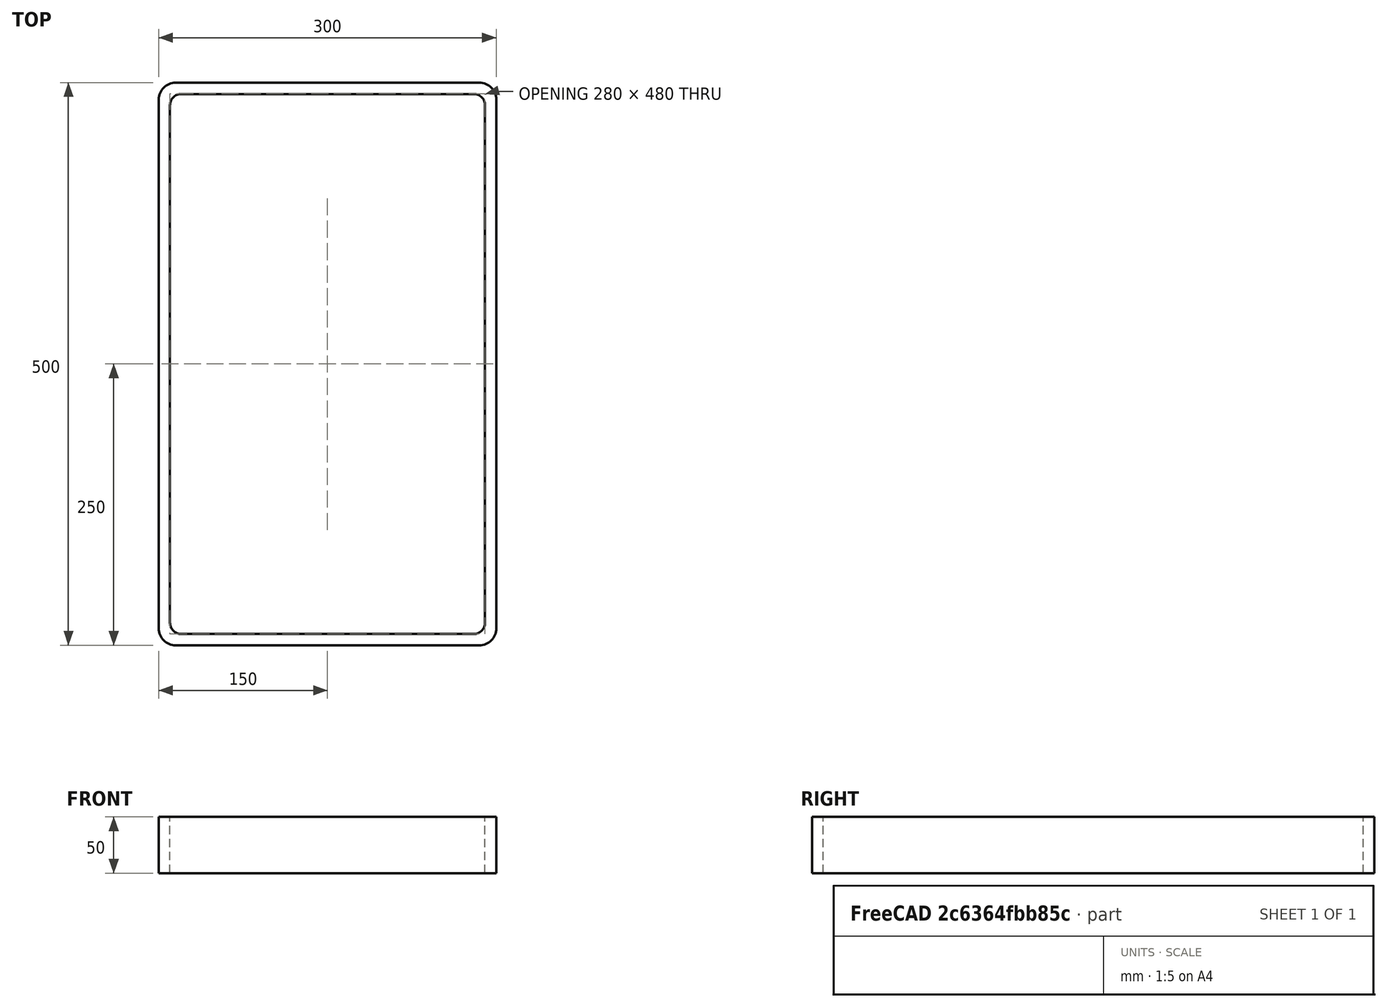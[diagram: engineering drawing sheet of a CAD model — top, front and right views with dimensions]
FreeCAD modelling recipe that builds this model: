
FCSTD DOCUMENT  (FreeCAD 0.15R4671 (Git))
Label: Rectangular hollow section 500x300x10 EN10219 S235JRH
License: All rights reserved
LicenseURL: http://en.wikipedia.org/wiki/All_rights_reserved
objects: Sketcher::SketchObject×1, Part::Extrusion×1
note: 2 computed .brp shape members not serialized (recipe doc carries the construction recipe); baked Part::Feature solids carry a one-line shape summary decoded from their .brp

FEATURE [Sketcher::SketchObject] Sketch
  sketch-geometry (16):
    g0: LineSegment StartX=-130 StartY=240 StartZ=0 EndX=130 EndY=240 EndZ=0
    g1: LineSegment StartX=140 StartY=230 StartZ=0 EndX=140 EndY=-230 EndZ=0
    g2: LineSegment StartX=130 StartY=-240 StartZ=0 EndX=-130 EndY=-240 EndZ=0
    g3: LineSegment StartX=-140 StartY=-230 StartZ=0 EndX=-140 EndY=230 EndZ=0
    g4: LineSegment StartX=-135 StartY=250 StartZ=0 EndX=135 EndY=250 EndZ=0
    g5: LineSegment StartX=150 StartY=235 StartZ=0 EndX=150 EndY=-235 EndZ=0
    g6: LineSegment StartX=135 StartY=-250 StartZ=0 EndX=-135 EndY=-250 EndZ=0
    g7: LineSegment StartX=-150 StartY=-235 StartZ=0 EndX=-150 EndY=235 EndZ=0
    g8: ArcOfCircle CenterX=-130 CenterY=230 CenterZ=0 NormalX=0 NormalY=0 NormalZ=1 Radius=10 StartAngle=1.5708 EndAngle=3.14159
    g9: ArcOfCircle CenterX=130 CenterY=230 CenterZ=0 NormalX=0 NormalY=0 NormalZ=1 Radius=10 StartAngle=0 EndAngle=1.5708
    g10: ArcOfCircle CenterX=130 CenterY=-230 CenterZ=0 NormalX=0 NormalY=0 NormalZ=1 Radius=10 StartAngle=4.71239 EndAngle=6.28319
    g11: ArcOfCircle CenterX=-130 CenterY=-230 CenterZ=0 NormalX=0 NormalY=0 NormalZ=1 Radius=10 StartAngle=3.14159 EndAngle=4.71239
    g12: ArcOfCircle CenterX=135 CenterY=235 CenterZ=0 NormalX=0 NormalY=0 NormalZ=1 Radius=15 StartAngle=0 EndAngle=1.5708
    g13: ArcOfCircle CenterX=135 CenterY=-235 CenterZ=0 NormalX=0 NormalY=0 NormalZ=1 Radius=15 StartAngle=4.71239 EndAngle=6.28319
    g14: ArcOfCircle CenterX=-135 CenterY=-235 CenterZ=0 NormalX=0 NormalY=0 NormalZ=1 Radius=15 StartAngle=3.14159 EndAngle=4.71239
    g15: ArcOfCircle CenterX=-135 CenterY=235 CenterZ=0 NormalX=0 NormalY=0 NormalZ=1 Radius=15 StartAngle=1.5708 EndAngle=3.14159
  constraints (36):
    c: Horizontal(g2)
    c: Vertical(g3)
    c: Horizontal(g6)
    c: Vertical(g7)
    c: Tangent(g3,g8) = 1.5708
    c: Tangent(g0,g8) = 1.5708
    c: Tangent(g0,g9) = 1.5708
    c: Tangent(g1,g9) = 1.5708
    c: Tangent(g1,g10) = 1.5708
    c: Tangent(g2,g10) = 1.5708
    c: Tangent(g2,g11) = 1.5708
    c: Tangent(g3,g11) = 1.5708
    c: Tangent(g4,g12) = 1.5708
    c: Tangent(g5,g12) = 1.5708
    c: Tangent(g5,g13) = 1.5708
    c: Tangent(g6,g13) = 1.5708
    c: Tangent(g6,g14) = 1.5708
    c: Tangent(g7,g14) = 1.5708
    c: Tangent(g7,g15) = 1.5708
    c: Tangent(g4,g15) = 1.5708
    c: Equal(g9,g8)
    c: Equal(g9,g11)
    c: Equal(g9,g10)
    c: Equal(g12,g15)
    c: Equal(g12,g14)
    c: Equal(g12,g13)
    c: Symmetric(g4,g6,g-1)
    c: Symmetric(g7,g5,g-2)
    c: DistanceY(g4,g6) = -500
    c: DistanceX(g7,g5) = 300
    c: Symmetric(g3,g1,g-2)
    c: Symmetric(g0,g2,g-1)
    c: DistanceY(g0,g4) = 10
    c: DistanceX(g5,g1) = -10
    c: Radius(g9) = 10
    c: Radius(g12) = 15
FEATURE [Part::Extrusion] Extrude  label="Rectangular hollow section 500x300x10 EN10219 S235JRH"
  Base = -> Sketch
  Dir = (0,0,50)
  Solid = true
